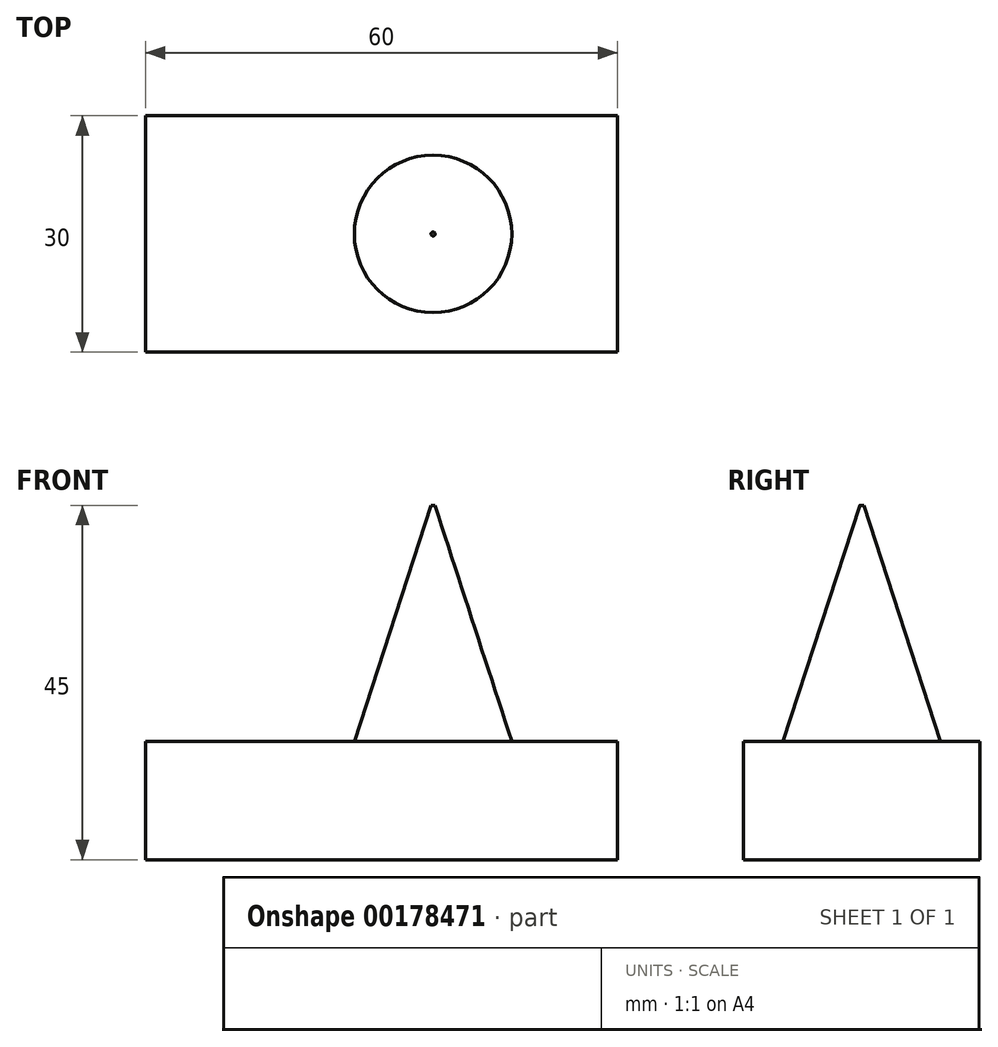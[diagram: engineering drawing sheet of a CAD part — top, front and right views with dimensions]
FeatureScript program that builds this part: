
annotation { "Feature Type Name" : "Feature", "Feature Type Description" : "" }
export const myFeature = defineFeature(function(context is Context, id is Id, definition is map)
    precondition{}
    {
        {
            var Q0;
            Q0=qCreatedBy(makeId("Top.planeOp"),FACE);
            var sketch = newSketch(context, id + "F0", { "sketchPlane" : qUnion([Q0])});
            skLineSegment(sketch, "E0.bottom", {"start": v(0, 0) * mm, "end": v(60, 0) * mm});
            skLineSegment(sketch, "E0.top", {"start": v(0, 30) * mm, "end": v(60, 30) * mm});
            skLineSegment(sketch, "E0.left", {"start": v(0, 0) * mm, "end": v(0, 30) * mm});
            skLineSegment(sketch, "E0.right", {"start": v(60, 0) * mm, "end": v(60, 30) * mm});
            skSolve(sketch);
        }
        {
            var Q0;
            Q0 = qSketchRegion(id + "F0", true);
            extrude(context, id + "F1", {"entities" : qUnion([Q0]), "depth" : 15 * mm});
        }
        {
            var Q0;
            Q0=makeQuery(id+"F1.opExtrude","CAP_FACE",FACE,{"disambiguationData":[OSD([sQuery(id+"F0.wireOp",EDGE,"E0.bottom"),sQuery(id+"F0.wireOp",EDGE,"E0.top"),sQuery(id+"F0.wireOp",EDGE,"E0.left"),sQuery(id+"F0.wireOp",EDGE,"E0.right")])],"isStart":false});
            var sketch = newSketch(context, id + "F2", { "sketchPlane" : qUnion([Q0])});
            skCircle(sketch, "E1", {"center": v(36.55, 15) * mm, "radius": 10 * mm});
            skPoint(sketch, "E1.centerSnap0", {"position": v(60, 15) * mm});
            skSolve(sketch);
        }
        {
            var Q0;
            Q0 = qSketchRegion(id + "F2", true);
            extrude(context, id + "F3", {"entities" : qUnion([Q0]), "operationType" : NewBodyOperationType.ADD, "depth" : 30 * mm, "hasDraft" : true, "draftAngle" : 18 * degree, "draftPullDirection" : true, "hasSecondDirectionDraft" : true, "secondDirectionDraftAngle" : 3 * degree});
        }
    });
